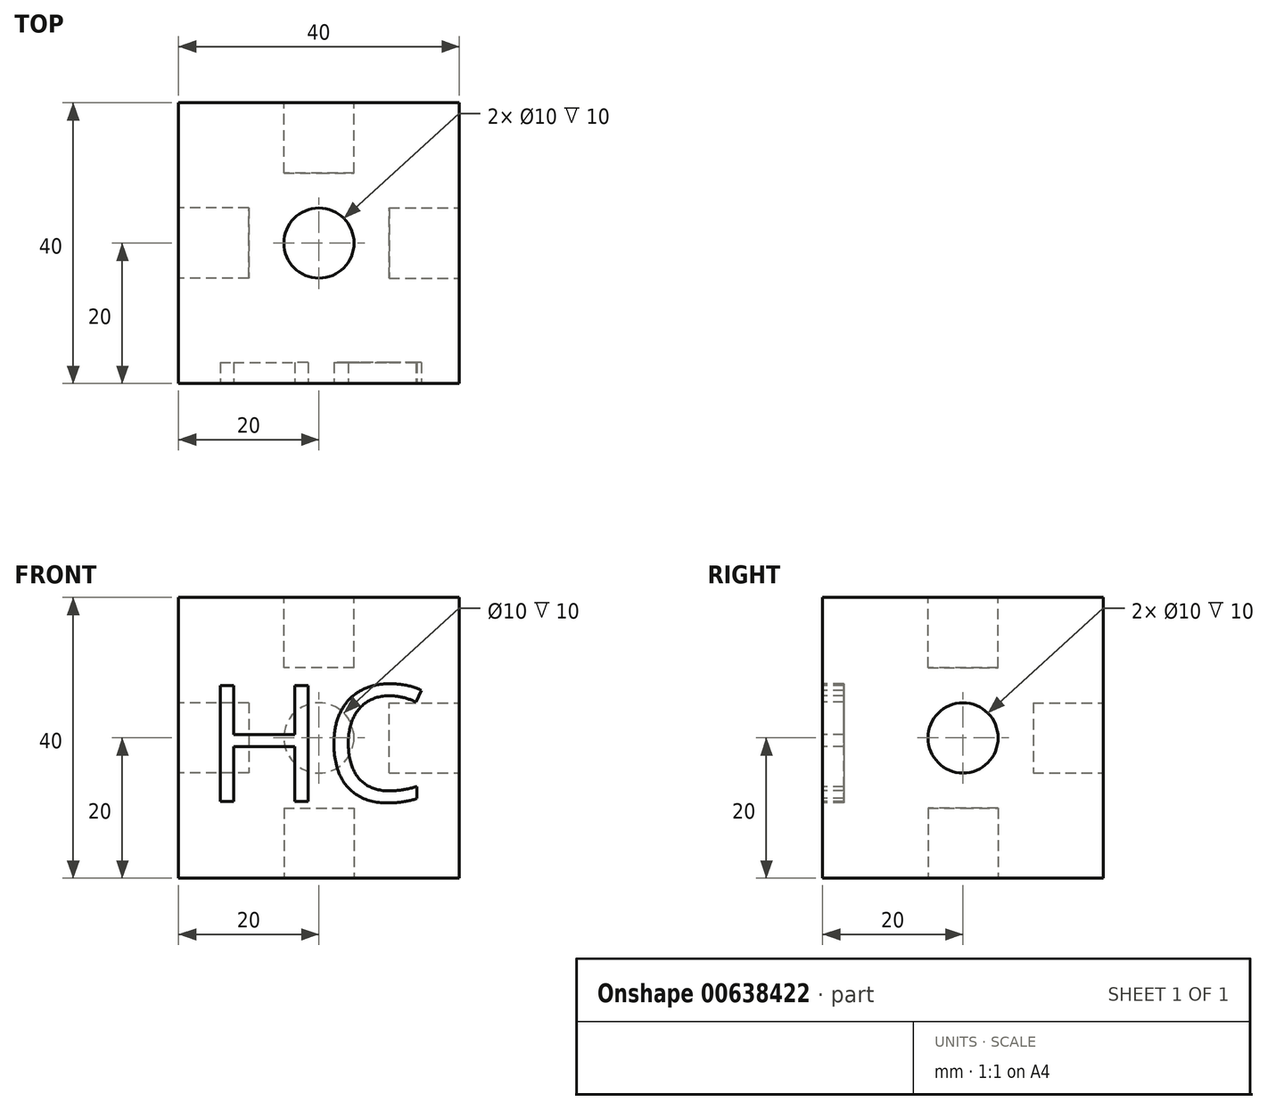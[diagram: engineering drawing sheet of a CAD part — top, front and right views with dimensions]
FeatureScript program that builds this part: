
annotation { "Feature Type Name" : "Feature", "Feature Type Description" : "" }
export const myFeature = defineFeature(function(context is Context, id is Id, definition is map)
    precondition{}
    {
        {
            var Q0;
            Q0=qCreatedBy(makeId("Front.planeOp"),FACE);
            var sketch = newSketch(context, id + "F0", { "sketchPlane" : qUnion([Q0])});
            skLineSegment(sketch, "E0", {"start": v(0, 0) * mm, "end": v(0, 40) * mm});
            skLineSegment(sketch, "E1", {"start": v(0, 40) * mm, "end": v(-40, 40) * mm});
            skLineSegment(sketch, "E2", {"start": v(-40, 40) * mm, "end": v(-40, 0) * mm});
            skLineSegment(sketch, "E3", {"start": v(-40, 0) * mm, "end": v(0, 0) * mm});
            skSolve(sketch);
        }
        {
            var Q0;
            Q0=makeQuery(id+"F0.imprint","IMPRINT",FACE,{"disambiguationData":[TD([[makeQuery(id+"F0.imprint","IMPRINT",EDGE,{"derivedFrom":sQuery(id+"F0.wireOp",EDGE,"E0")}),1.0]])]});
            extrude(context, id + "F1", {"entities" : qUnion([Q0]), "depth" : 40 * mm, "offsetDistance" : 25 * mm});
        }
        {
            var Q0;
            Q0=makeQuery(id+"F1.opExtrude","CAP_FACE",FACE,{"disambiguationData":[OSD([sQuery(id+"F0.wireOp",EDGE,"E0"),sQuery(id+"F0.wireOp",EDGE,"E1"),sQuery(id+"F0.wireOp",EDGE,"E2"),sQuery(id+"F0.wireOp",EDGE,"E3")])],"isStart":false});
            var sketch = newSketch(context, id + "F2", { "sketchPlane" : qUnion([Q0])});
            skText(sketch, "E4", { "text": "HC", "fontName": "OpenSans-Regular.ttf"});
            const initialGuessF2  = {"E4": [-0.03634, 0.01097, 1, 0, 0.01665]};
            skSetInitialGuess(sketch, initialGuessF2);
            skSolve(sketch);
        }
        {
            var Q0;
            Q0 = qSketchRegion(id + "F2", true);
            extrude(context, id + "F3", {"entities" : qUnion([Q0]), "operationType" : NewBodyOperationType.REMOVE, "oppositeDirection" : true, "depth" : 3 * mm, "offsetDistance" : 25 * mm});
        }
        {
            var Q0;
            Q0=makeQuery(id+"F1.opExtrude","SWEPT_FACE",FACE,{"disambiguationData":[OSD([sQuery(id+"F0.wireOp",EDGE,"E0")])]});
            var sketch = newSketch(context, id + "F4", { "sketchPlane" : qUnion([Q0])});
            skCircle(sketch, "E5", {"center": v(-20, 20) * mm, "radius": 5 * mm});
            skPoint(sketch, "E5.centerSnap0", {"position": v(-20, 40) * mm});
            skPoint(sketch, "E5.centerSnap1", {"position": v(-40, 20) * mm});
            skSolve(sketch);
        }
        {
            var Q0;
            Q0 = qSketchRegion(id + "F4", true);
            extrude(context, id + "F5", {"entities" : qUnion([Q0]), "operationType" : NewBodyOperationType.REMOVE, "oppositeDirection" : true, "depth" : 10 * mm, "offsetDistance" : 25 * mm});
        }
        {
            var Q0;
            Q0=makeQuery(id+"F1.opExtrude","SWEPT_FACE",FACE,{"disambiguationData":[OSD([sQuery(id+"F0.wireOp",EDGE,"E2")])]});
            var sketch = newSketch(context, id + "F6", { "sketchPlane" : qUnion([Q0])});
            skCircle(sketch, "E6", {"center": v(20, 20) * mm, "radius": 5 * mm});
            skPoint(sketch, "E6.centerSnap0", {"position": v(20, 40) * mm});
            skPoint(sketch, "E6.centerSnap1", {"position": v(0, 20) * mm});
            skSolve(sketch);
        }
        {
            var Q0;
            Q0 = qSketchRegion(id + "F6", true);
            extrude(context, id + "F7", {"entities" : qUnion([Q0]), "operationType" : NewBodyOperationType.REMOVE, "oppositeDirection" : true, "depth" : 10 * mm, "offsetDistance" : 25 * mm});
        }
        {
            var Q0;
            Q0=makeQuery(id+"F1.opExtrude","SWEPT_FACE",FACE,{"disambiguationData":[OSD([sQuery(id+"F0.wireOp",EDGE,"E1")])]});
            var sketch = newSketch(context, id + "F8", { "sketchPlane" : qUnion([Q0])});
            skCircle(sketch, "E7", {"center": v(-20, -20) * mm, "radius": 5 * mm});
            skPoint(sketch, "E7.centerSnap0", {"position": v(-20, 0) * mm});
            skPoint(sketch, "E7.centerSnap1", {"position": v(-40, -20) * mm});
            skSolve(sketch);
        }
        {
            var Q0;
            Q0 = qSketchRegion(id + "F8", true);
            extrude(context, id + "F9", {"entities" : qUnion([Q0]), "operationType" : NewBodyOperationType.REMOVE, "oppositeDirection" : true, "depth" : 10 * mm, "offsetDistance" : 25 * mm});
        }
        {
            var Q0;
            Q0=makeQuery(id+"F1.opExtrude","SWEPT_FACE",FACE,{"disambiguationData":[OSD([sQuery(id+"F0.wireOp",EDGE,"E3")])]});
            var sketch = newSketch(context, id + "F10", { "sketchPlane" : qUnion([Q0])});
            skCircle(sketch, "E8", {"center": v(-20, 20) * mm, "radius": 5 * mm});
            skPoint(sketch, "E8.centerSnap0", {"position": v(-20, 40) * mm});
            skPoint(sketch, "E8.centerSnap1", {"position": v(-40, 20) * mm});
            skSolve(sketch);
        }
        {
            var Q0;
            Q0 = qSketchRegion(id + "F10", true);
            extrude(context, id + "F11", {"entities" : qUnion([Q0]), "operationType" : NewBodyOperationType.REMOVE, "oppositeDirection" : true, "depth" : 10 * mm, "offsetDistance" : 25 * mm});
        }
        {
            var Q0;
            Q0=makeQuery(id+"F1.opExtrude","CAP_FACE",FACE,{"disambiguationData":[OSD([sQuery(id+"F0.wireOp",EDGE,"E0"),sQuery(id+"F0.wireOp",EDGE,"E1"),sQuery(id+"F0.wireOp",EDGE,"E2"),sQuery(id+"F0.wireOp",EDGE,"E3")])],"isStart":true});
            var sketch = newSketch(context, id + "F12", { "sketchPlane" : qUnion([Q0])});
            skCircle(sketch, "E9", {"center": v(20, 20) * mm, "radius": 5 * mm});
            skPoint(sketch, "E9.centerSnap0", {"position": v(20, 40) * mm});
            skPoint(sketch, "E9.centerSnap1", {"position": v(0, 20) * mm});
            skSolve(sketch);
        }
        {
            var Q0;
            Q0 = qSketchRegion(id + "F12", true);
            extrude(context, id + "F13", {"entities" : qUnion([Q0]), "operationType" : NewBodyOperationType.REMOVE, "oppositeDirection" : true, "depth" : 10 * mm, "offsetDistance" : 25 * mm});
        }
    });
